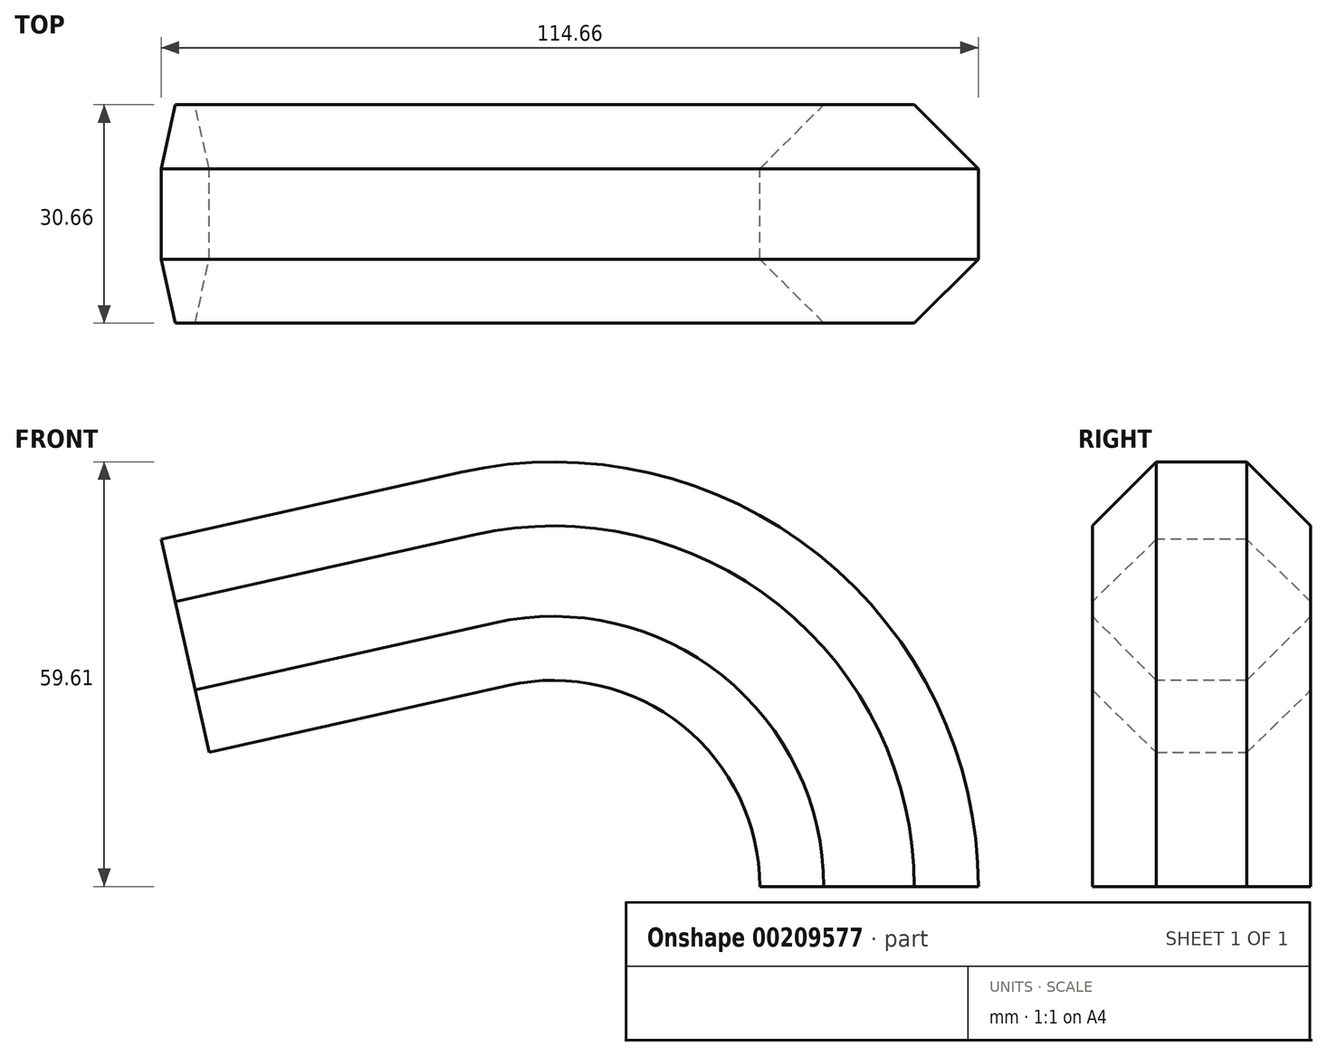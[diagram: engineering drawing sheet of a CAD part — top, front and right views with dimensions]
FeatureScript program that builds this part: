
annotation { "Feature Type Name" : "Feature", "Feature Type Description" : "" }
export const myFeature = defineFeature(function(context is Context, id is Id, definition is map)
    precondition{}
    {
        {
            var Q0;
            Q0=qCreatedBy(makeId("Top.planeOp"),FACE);
            var sketch = newSketch(context, id + "F0", { "sketchPlane" : qUnion([Q0])});
            skCircle(sketch, "E0.cCircle", {"center": v(0, 0) * mm, "radius": 15.33 * mm, "construction": true});
            skLineSegment(sketch, "E0.0", {"start": v(-6.35, 15.33) * mm, "end": v(6.35, 15.33) * mm});
            skLineSegment(sketch, "E0.1", {"start": v(6.35, 15.33) * mm, "end": v(15.33, 6.35) * mm});
            skLineSegment(sketch, "E0.2", {"start": v(15.33, 6.35) * mm, "end": v(15.33, -6.35) * mm});
            skLineSegment(sketch, "E0.3", {"start": v(15.33, -6.35) * mm, "end": v(6.35, -15.33) * mm});
            skLineSegment(sketch, "E0.4", {"start": v(6.35, -15.33) * mm, "end": v(-6.35, -15.33) * mm});
            skLineSegment(sketch, "E0.5", {"start": v(-6.35, -15.33) * mm, "end": v(-15.33, -6.35) * mm});
            skLineSegment(sketch, "E0.6", {"start": v(-15.33, -6.35) * mm, "end": v(-15.33, 6.35) * mm});
            skLineSegment(sketch, "E0.7", {"start": v(-15.33, 6.35) * mm, "end": v(-6.35, 15.33) * mm});
            skPoint(sketch, "E0.0.midPoint", {"position": v(0, 15.33) * mm});
            skSolve(sketch);
        }
        {
            var Q0;
            Q0=qCreatedBy(makeId("Front.planeOp"),FACE);
            var sketch = newSketch(context, id + "F1", { "sketchPlane" : qUnion([Q0])});
            skArc(sketch, "E1", {"start": v(0, 0) * mm, "mid": v(-16.61, 34.57) * mm, "end": v(-53.98, 43.2) * mm});
            skLineSegment(sketch, "E2", {"start": v(0, 0) * mm, "end": v(-92.74, 0) * mm, "construction": true});
            skLineSegment(sketch, "E3", {"start": v(-53.98, 43.2) * mm, "end": v(-95.97, 33.79) * mm});
            skSolve(sketch);
        }
        {
            var Q0;
            Q0 = qSketchRegion(id + "F0", true);
            var Q1;
            Q1 = qConstructionFilter(qBodyType(qCreatedBy(id + "F1" ,EDGE), BodyType.WIRE), ConstructionObject.NO);
            sweep(context, id + "F2", {"profiles" : qUnion([Q0]), "path" : qUnion([Q1])});
        }
    });
